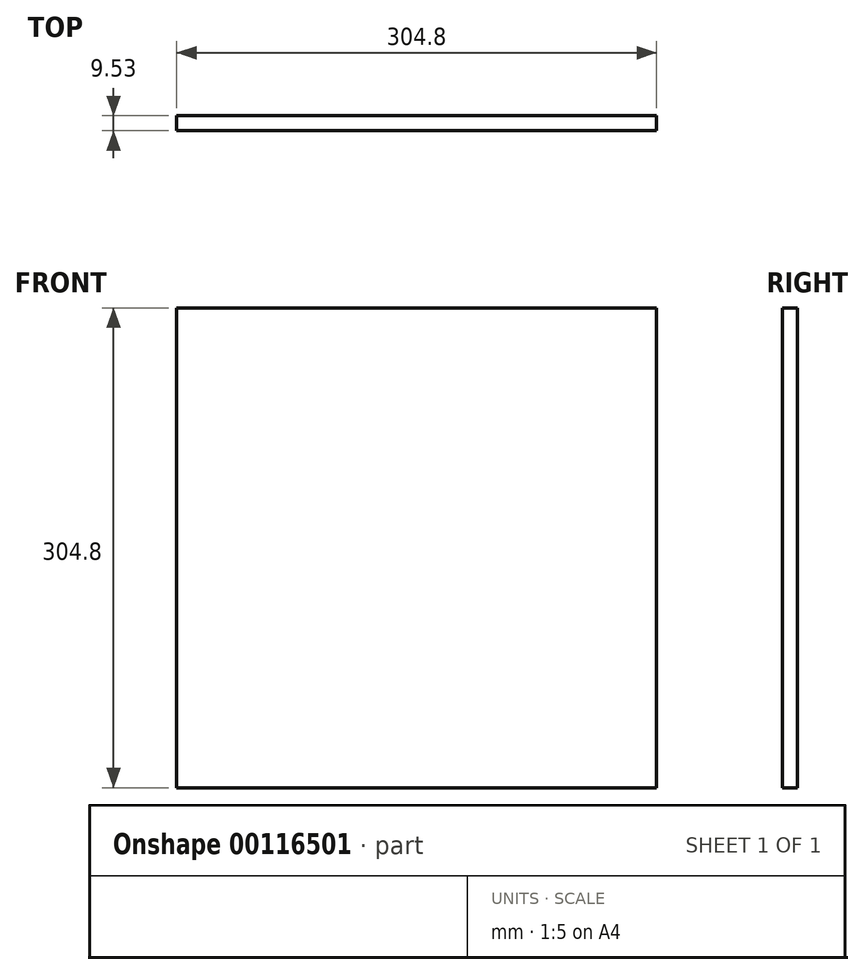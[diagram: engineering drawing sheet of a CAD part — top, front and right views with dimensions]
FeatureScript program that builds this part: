
annotation { "Feature Type Name" : "Feature", "Feature Type Description" : "" }
export const myFeature = defineFeature(function(context is Context, id is Id, definition is map)
    precondition{}
    {
        {
            var Q0;
            Q0=qCreatedBy(makeId("Front.planeOp"),FACE);
            var sketch = newSketch(context, id + "F0", { "sketchPlane" : qUnion([Q0])});
            skLineSegment(sketch, "E0.bottom", {"start": v(0, 0) * mm, "end": v(304.8, 0) * mm});
            skLineSegment(sketch, "E0.top", {"start": v(0, 304.8) * mm, "end": v(304.8, 304.8) * mm});
            skLineSegment(sketch, "E0.left", {"start": v(0, 0) * mm, "end": v(0, 304.8) * mm});
            skLineSegment(sketch, "E0.right", {"start": v(304.8, 0) * mm, "end": v(304.8, 304.8) * mm});
            skSolve(sketch);
        }
        {
            var Q0;
            Q0=makeQuery(id+"F0.imprint","IMPRINT",FACE,{"disambiguationData":[TD([[makeQuery(id+"F0.imprint","IMPRINT",EDGE,{"derivedFrom":sQuery(id+"F0.wireOp",EDGE,"E0.bottom")}),1.0]])]});
            extrude(context, id + "F1", {"entities" : qUnion([Q0]), "depth" : 9.52 * mm});
        }
    });
